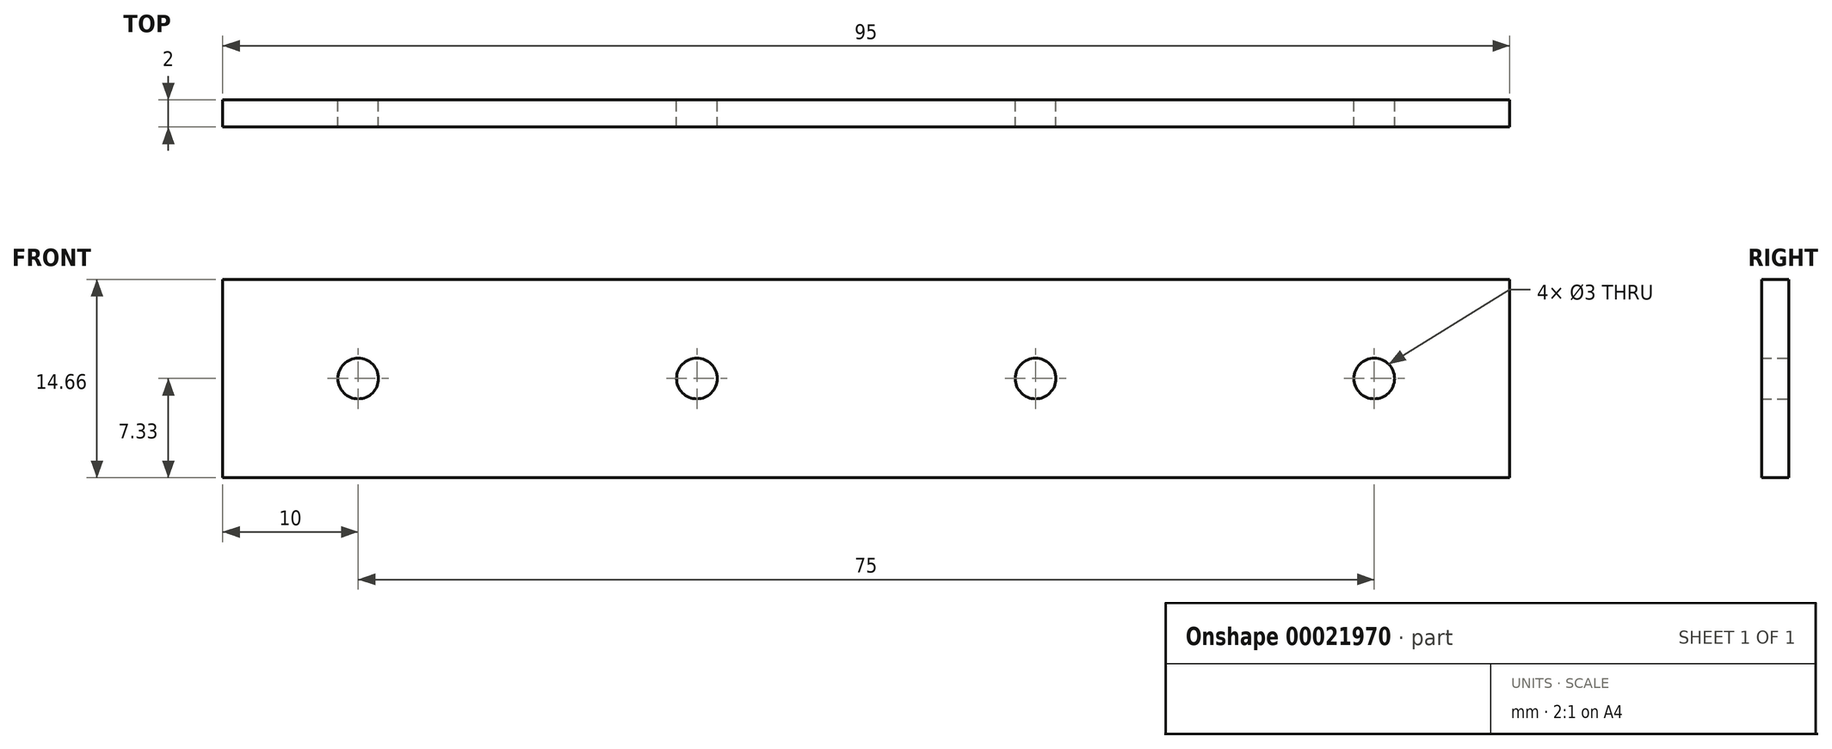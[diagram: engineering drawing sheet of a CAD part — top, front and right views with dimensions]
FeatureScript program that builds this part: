
annotation { "Feature Type Name" : "Feature", "Feature Type Description" : "" }
export const myFeature = defineFeature(function(context is Context, id is Id, definition is map)
    precondition{}
    {
        {
            var Q0;
            Q0=qCreatedBy(makeId("Front.planeOp"),FACE);
            var sketch = newSketch(context, id + "F0", { "sketchPlane" : qUnion([Q0])});
            skLineSegment(sketch, "E0.rect.bottom", {"start": v(47.5, 7.33) * mm, "end": v(-47.5, 7.33) * mm});
            skLineSegment(sketch, "E0.rect.top", {"start": v(47.5, -7.33) * mm, "end": v(-47.5, -7.33) * mm});
            skLineSegment(sketch, "E0.rect.left", {"start": v(47.5, 7.33) * mm, "end": v(47.5, -7.33) * mm});
            skLineSegment(sketch, "E0.rect.right", {"start": v(-47.5, 7.33) * mm, "end": v(-47.5, -7.33) * mm});
            skPoint(sketch, "E0.rect.middle", {"position": v(0, 0) * mm});
            skCircle(sketch, "E1", {"center": v(-12.5, 0) * mm, "radius": 1.5 * mm});
            skCircle(sketch, "E2", {"center": v(12.5, 0) * mm, "radius": 1.5 * mm});
            skCircle(sketch, "E3", {"center": v(-37.5, 0) * mm, "radius": 1.5 * mm});
            skCircle(sketch, "E4", {"center": v(37.5, 0) * mm, "radius": 1.5 * mm});
            skSolve(sketch);
        }
        {
            var Q0;
            Q0 = qSketchRegion(id + "F0", true);
            var Q1;
            Q1=makeQuery(id+"F0.imprint","IMPRINT",FACE,{"disambiguationData":[TD([[makeQuery(id+"F0.imprint","IMPRINT",EDGE,{"derivedFrom":sQuery(id+"F0.wireOp",EDGE,"E0.rect.bottom")}),1.0]])]});
            extrude(context, id + "F1", {"entities" : qUnion([Q0, Q1]), "depth" : 2 * mm});
        }
    });
